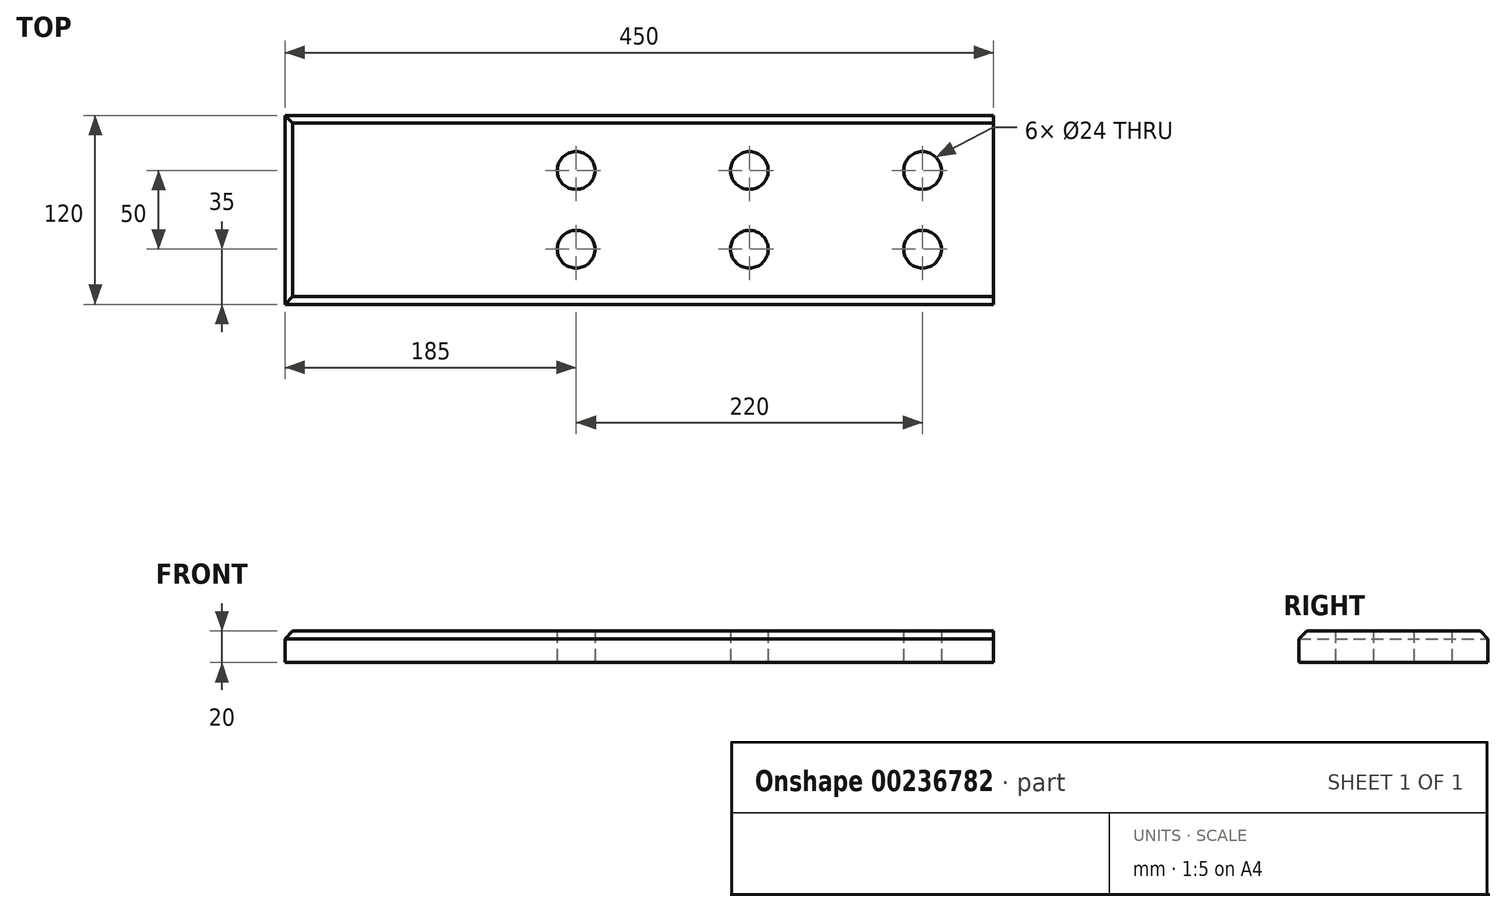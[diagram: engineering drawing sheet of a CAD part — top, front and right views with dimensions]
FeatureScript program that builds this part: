
annotation { "Feature Type Name" : "Feature", "Feature Type Description" : "" }
export const myFeature = defineFeature(function(context is Context, id is Id, definition is map)
    precondition{}
    {
        {
            var Q0;
            Q0=qCreatedBy(makeId("Top.planeOp"),FACE);
            var sketch = newSketch(context, id + "F0", { "sketchPlane" : qUnion([Q0])});
            skLineSegment(sketch, "E0.bottom", {"start": v(0, 0) * mm, "end": v(450, 0) * mm});
            skLineSegment(sketch, "E0.top", {"start": v(0, 120) * mm, "end": v(450, 120) * mm});
            skLineSegment(sketch, "E0.left", {"start": v(0, 0) * mm, "end": v(0, 120) * mm});
            skLineSegment(sketch, "E0.right", {"start": v(450, 0) * mm, "end": v(450, 120) * mm});
            skSolve(sketch);
        }
        {
            var Q0;
            Q0 = qSketchRegion(id + "F0", true);
            extrude(context, id + "F1", {"entities" : qUnion([Q0]), "depth" : 20 * mm, "offsetDistance" : 25 * mm});
        }
        {
            var Q0;
            Q0=makeQuery(id+"F1.opExtrude","CAP_FACE",FACE,{"disambiguationData":[OSD([sQuery(id+"F0.wireOp",EDGE,"E0.bottom"),sQuery(id+"F0.wireOp",EDGE,"E0.top"),sQuery(id+"F0.wireOp",EDGE,"E0.left"),sQuery(id+"F0.wireOp",EDGE,"E0.right")])],"isStart":false});
            var sketch = newSketch(context, id + "F2", { "sketchPlane" : qUnion([Q0])});
            skPoint(sketch, "E1", {"position": v(185, 85) * mm});
            skPoint(sketch, "E2", {"position": v(295, 85) * mm});
            skPoint(sketch, "E3", {"position": v(405, 85) * mm});
            skPoint(sketch, "E4", {"position": v(405, 35) * mm});
            skPoint(sketch, "E5", {"position": v(295, 35) * mm});
            skPoint(sketch, "E6", {"position": v(185, 35) * mm});
            skSolve(sketch);
        }
        {
            var Q0;
            Q0=sQuery(id+"F2.wireOp",VERTEX,"E1");
            var Q1;
            Q1=sQuery(id+"F2.wireOp",VERTEX,"E6");
            var Q2;
            Q2=sQuery(id+"F2.wireOp",VERTEX,"E2");
            var Q3;
            Q3=sQuery(id+"F2.wireOp",VERTEX,"E5");
            var Q4;
            Q4=sQuery(id+"F2.wireOp",VERTEX,"E3");
            var Q5;
            Q5=sQuery(id+"F2.wireOp",VERTEX,"E4");
            var Q6;
            Q6=makeQuery(id+"F1.opExtrude","SWEPT_BODY",BODY,{"disambiguationData":[OSD([sQuery(id+"F0.wireOp",EDGE,"E0.bottom"),sQuery(id+"F0.wireOp",EDGE,"E0.top"),sQuery(id+"F0.wireOp",EDGE,"E0.left"),sQuery(id+"F0.wireOp",EDGE,"E0.right")])]});
            hole(context, id + "F3", {"style" : HoleStyle.SIMPLE, "endStyle" : HoleEndStyle.THROUGH, "standardTappedOrClearance" : lookupTablePath({ "fit" : "Normal", "standard" : "ISO", "size" : "M22", "type" : "Clearance" }), "standardBlindInLast" : lookupTablePath({ "fit" : "Normal", "standard" : "ISO", "engagement" : "75%", "pitch" : "1.5 mm", "size" : "M22", "type" : "Clearance & tapped" }), "holeDiameter" : 24 * mm, "majorDiameter" : 5 * mm, "isTappedThrough" : true, "tappedDepth" : 31.25 * mm, "tapClearance" : 3, "startFromSketch" : true, "locations" : qUnion([Q0, Q1, Q2, Q3, Q4, Q5]), "scope" : qUnion([Q6])});
        }
        {
            var Q0;
            Q0=makeQuery(id+"F1.opExtrude","CAP_EDGE",EDGE,{"disambiguationData":[OSD([sQuery(id+"F0.wireOp",EDGE,"E0.top")])],"isStart":false});
            var Q1;
            Q1=makeQuery(id+"F1.opExtrude","CAP_EDGE",EDGE,{"disambiguationData":[OSD([sQuery(id+"F0.wireOp",EDGE,"E0.bottom")])],"isStart":false});
            var Q2;
            Q2=makeQuery(id+"F1.opExtrude","CAP_EDGE",EDGE,{"disambiguationData":[OSD([sQuery(id+"F0.wireOp",EDGE,"E0.left")])],"isStart":false});
            chamfer(context, id + "F4", {"entities" : qUnion([Q0, Q1, Q2]), "width" : 5 * mm, "tangentPropagation" : true});
        }
    });
